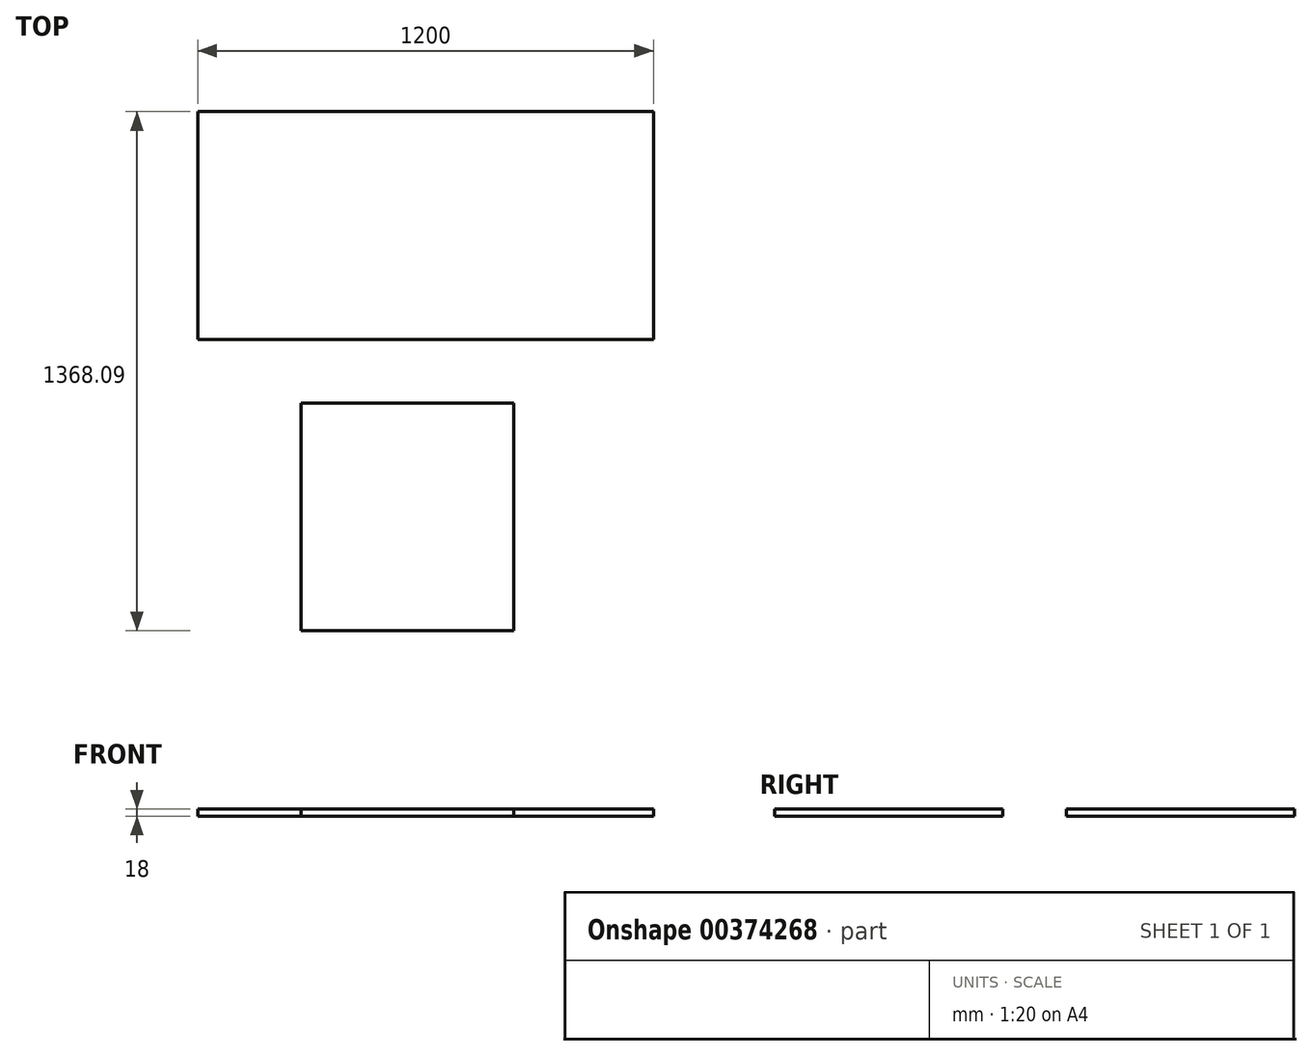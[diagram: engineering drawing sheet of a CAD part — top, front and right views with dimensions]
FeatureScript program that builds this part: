
annotation { "Feature Type Name" : "Feature", "Feature Type Description" : "" }
export const myFeature = defineFeature(function(context is Context, id is Id, definition is map)
    precondition{}
    {
        {
            var Q0;
            Q0=qCreatedBy(makeId("Top.planeOp"),FACE);
            var sketch = newSketch(context, id + "F0", { "sketchPlane" : qUnion([Q0])});
            skLineSegment(sketch, "E0.bottom", {"start": v(600, 300) * mm, "end": v(-600, 300) * mm});
            skLineSegment(sketch, "E0.top", {"start": v(600, -300) * mm, "end": v(-600, -300) * mm});
            skLineSegment(sketch, "E0.left", {"start": v(600, 300) * mm, "end": v(600, -300) * mm});
            skLineSegment(sketch, "E0.right", {"start": v(-600, 300) * mm, "end": v(-600, -300) * mm});
            skPoint(sketch, "E0.middle", {"position": v(0, 0) * mm});
            skSolve(sketch);
        }
        {
            var Q0;
            Q0=makeQuery(id+"F0.imprint","IMPRINT",FACE,{"disambiguationData":[TD([[makeQuery(id+"F0.imprint","IMPRINT",EDGE,{"derivedFrom":sQuery(id+"F0.wireOp",EDGE,"E0.bottom")}),1.0]])]});
            extrude(context, id + "F1", {"entities" : qUnion([Q0]), "depth" : 18 * mm});
        }
        {
            var Q0;
            Q0=qCreatedBy(makeId("Top.planeOp"),FACE);
            var sketch = newSketch(context, id + "F2", { "sketchPlane" : qUnion([Q0])});
            skLineSegment(sketch, "E1.bottom", {"start": v(-328.03, -468.09) * mm, "end": v(231.97, -468.09) * mm});
            skLineSegment(sketch, "E1.top", {"start": v(-328.03, -1068.09) * mm, "end": v(231.97, -1068.09) * mm});
            skLineSegment(sketch, "E1.left", {"start": v(-328.03, -468.09) * mm, "end": v(-328.03, -1068.09) * mm});
            skLineSegment(sketch, "E1.right", {"start": v(231.97, -468.09) * mm, "end": v(231.97, -1068.09) * mm});
            skSolve(sketch);
        }
        {
            var Q0;
            Q0=makeQuery(id+"F2.imprint","IMPRINT",FACE,{"disambiguationData":[TD([[makeQuery(id+"F2.imprint","IMPRINT",EDGE,{"derivedFrom":sQuery(id+"F2.wireOp",EDGE,"E1.bottom")}),-1.0]])]});
            extrude(context, id + "F3", {"entities" : qUnion([Q0]), "depth" : 18 * mm});
        }
    });
